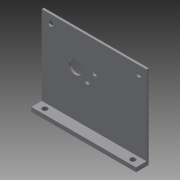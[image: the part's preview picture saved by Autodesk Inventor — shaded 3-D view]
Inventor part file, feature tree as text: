
AUTODESK INVENTOR PART (.ipt)
format: ipt  version: 2015 (Build 190159000, 159)  size: 124,416 bytes
history: native  units: in
note: dims shown in document units (in); Inventor stores cm internally (conversion verified against a paired STEP export)
features: sketch x6, extrude x3, hole x3
ambient origin geometry x8: Origin, YZ Plane, XZ Plane, XY Plane, X Axis, Y Axis, Z Axis, Center Point
bodies: Solid1 (feature_tree)
feature tree (12):
  extrude  "Extrusion1"  Depth=2.5in
  extrude  "Extrusion2"  Depth=0.1in
  hole  "Hole1"  [1 undecoded]
  hole  "Hole2"  [1 undecoded]
  hole  "Hole3"  [1 undecoded]
  extrude  "Extrusion3"  Depth=0.25in
  sketch  "Sketch1"  dims[d0=2.0in d1=2.5in]
  sketch  "Sketch2"  dims[d2=0.05in d3=0.0in d4=0.1in]
  sketch  "Sketch3"  dims[d5=0.25in d6=0.0in d7=0.7in]
  sketch  "Sketch4"  dims[d8=1.25in]
  sketch  "Sketch5"  dims[d9=0.125in d10=0.75in d11=0.375in d12=0.25in d13=0.5635in d14=1.0in d15=0.8108in d16=0.2in]
  sketch  "Sketch6"  dims[d17=0.2in d18=0.2in d19=0.2in d20=0.1254in d21=0.75in d22=0.375in d23=0.25in d24=0.5635in d25=1.0in d26=0.8108in d27=0.125in d28=0.2in d29=0.125in d30=0.2in d31=0.1254in d32=0.75in d33=0.375in d34=0.25in d35=0.5635in d36=1.0in d37=0.8108in d38=0.3125in d39=0.3125in d42=0.32in d43=0.125in d44=1.0in d45=0.0in d46=0.6in d47=0.6in d48=1.0419in d49=1.0739in]
note: 3 required parameter values undecoded (feature->parameter linkage not recoverable at this tier; creation-order binding heuristic only, values carry confidence <= 0.55)
